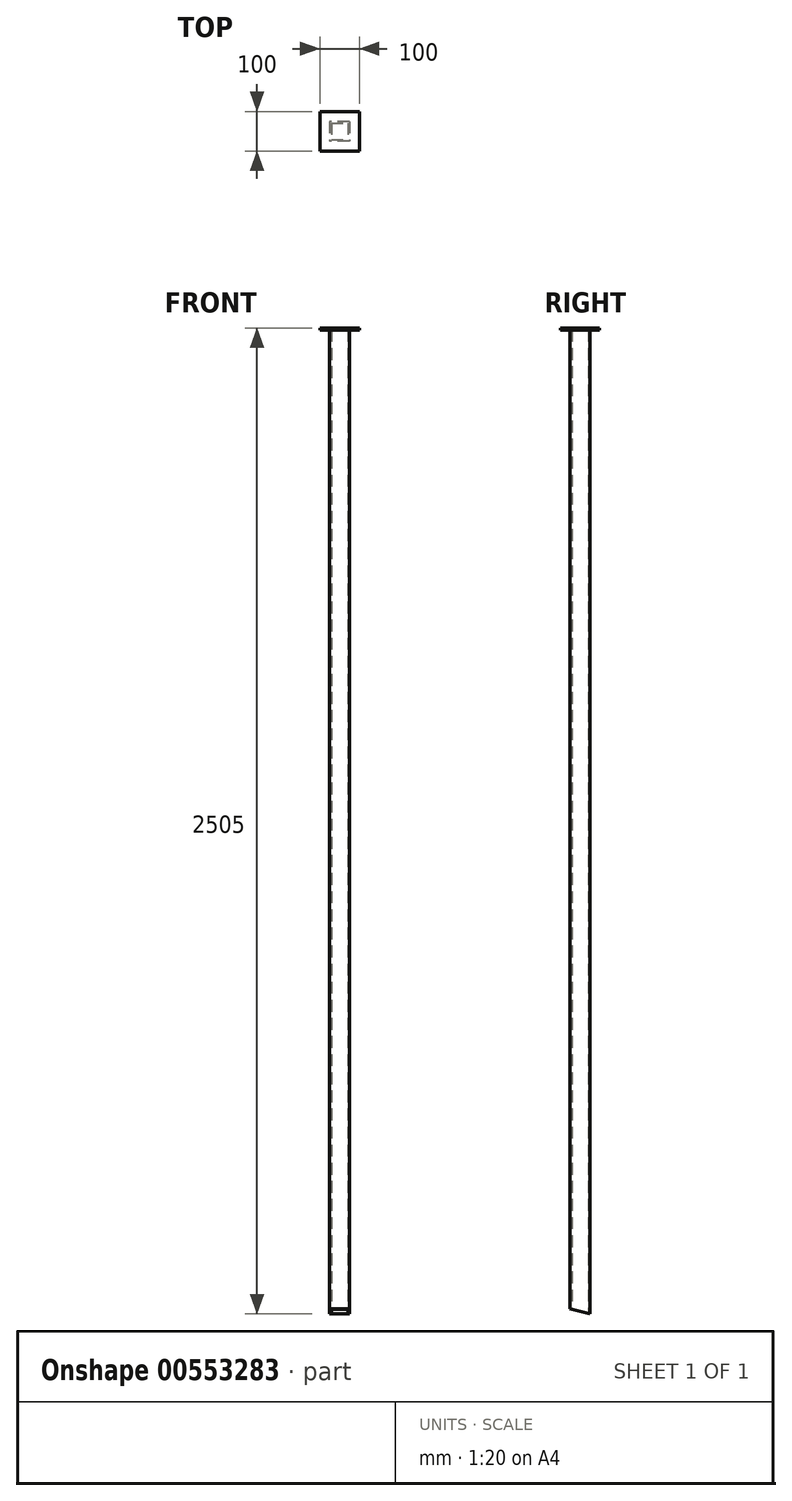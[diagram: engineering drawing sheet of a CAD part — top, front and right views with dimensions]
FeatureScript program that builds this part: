
annotation { "Feature Type Name" : "Feature", "Feature Type Description" : "" }
export const myFeature = defineFeature(function(context is Context, id is Id, definition is map)
    precondition{}
    {
        {
            var Q0;
            Q0=qCreatedBy(makeId("Top.planeOp"),FACE);
            var sketch = newSketch(context, id + "F0", { "sketchPlane" : qUnion([Q0])});
            skLineSegment(sketch, "E0.bottom", {"start": v(25, -25) * mm, "end": v(-25, -25) * mm});
            skLineSegment(sketch, "E0.top", {"start": v(25, 25) * mm, "end": v(-25, 25) * mm});
            skLineSegment(sketch, "E0.left", {"start": v(25, -25) * mm, "end": v(25, 25) * mm});
            skLineSegment(sketch, "E0.right", {"start": v(-25, -25) * mm, "end": v(-25, 25) * mm});
            skPoint(sketch, "E0.middle", {"position": v(0, 0) * mm});
            skLineSegment(sketch, "E1.bottom", {"start": v(21, -21) * mm, "end": v(-21, -21) * mm});
            skLineSegment(sketch, "E1.top", {"start": v(21, 21) * mm, "end": v(-21, 21) * mm});
            skLineSegment(sketch, "E1.left", {"start": v(21, -21) * mm, "end": v(21, 21) * mm});
            skLineSegment(sketch, "E1.right", {"start": v(-21, -21) * mm, "end": v(-21, 21) * mm});
            skSolve(sketch);
        }
        {
            var Q0;
            Q0=makeQuery(id+"F0.imprint","IMPRINT",FACE,{"disambiguationData":[TD([[makeQuery(id+"F0.imprint","IMPRINT",EDGE,{"derivedFrom":sQuery(id+"F0.wireOp",EDGE,"E0.bottom")}),-1.0]])]});
            extrude(context, id + "F1", {"entities" : qUnion([Q0]), "depth" : 2500 * mm, "offsetDistance" : 25 * mm});
        }
        {
            var Q0;
            Q0=makeQuery(id+"F1.opExtrude","CAP_FACE",FACE,{"disambiguationData":[OSD([sQuery(id+"F0.wireOp",EDGE,"E0.bottom"),sQuery(id+"F0.wireOp",EDGE,"E0.top"),sQuery(id+"F0.wireOp",EDGE,"E0.left"),sQuery(id+"F0.wireOp",EDGE,"E0.right"),sQuery(id+"F0.wireOp",EDGE,"E1.bottom"),sQuery(id+"F0.wireOp",EDGE,"E1.top"),sQuery(id+"F0.wireOp",EDGE,"E1.left"),sQuery(id+"F0.wireOp",EDGE,"E1.right")])],"isStart":false});
            var sketch = newSketch(context, id + "F2", { "sketchPlane" : qUnion([Q0])});
            skLineSegment(sketch, "E2.bottom", {"start": v(50, 50) * mm, "end": v(-50, 50) * mm});
            skLineSegment(sketch, "E2.top", {"start": v(50, -50) * mm, "end": v(-50, -50) * mm});
            skLineSegment(sketch, "E2.left", {"start": v(50, 50) * mm, "end": v(50, -50) * mm});
            skLineSegment(sketch, "E2.right", {"start": v(-50, 50) * mm, "end": v(-50, -50) * mm});
            skPoint(sketch, "E2.middle", {"position": v(0, 0) * mm});
            skSolve(sketch);
        }
        {
            var Q0;
            Q0=makeQuery(id+"F2.imprint","IMPRINT",FACE,{"disambiguationData":[TD([[makeQuery(id+"F2.imprint","IMPRINT",EDGE,{"derivedFrom":sQuery(id+"F2.wireOp",EDGE,"E2.bottom")}),1.0]])]});
            var Q1;
            Q1=makeQuery(id+"F2.imprint","IMPRINT",FACE,{"disambiguationData":[TD([[makeQuery(id+"F2.imprint","IMPRINT",EDGE,{"derivedFrom":makeQuery(id+"F1.opExtrude","CAP_EDGE",EDGE,{"disambiguationData":[OSD([sQuery(id+"F0.wireOp",EDGE,"E0.bottom")])],"isStart":false})}),-1.0]])]});
            var Q2;
            Q2=makeQuery(id+"F2.imprint","IMPRINT",FACE,{"disambiguationData":[TD([[makeQuery(id+"F2.imprint","IMPRINT",EDGE,{"derivedFrom":makeQuery(id+"F1.opExtrude","CAP_EDGE",EDGE,{"disambiguationData":[OSD([sQuery(id+"F0.wireOp",EDGE,"E1.bottom")])],"isStart":false})}),-1.0]])]});
            extrude(context, id + "F3", {"entities" : qUnion([Q0, Q1, Q2]), "operationType" : NewBodyOperationType.ADD, "depth" : 5 * mm, "offsetDistance" : 25 * mm});
        }
        {
            var Q0;
            Q0=makeQuery(id+"F1.opExtrude","SWEPT_FACE",FACE,{"disambiguationData":[OSD([sQuery(id+"F0.wireOp",EDGE,"E0.right")])]});
            var sketch = newSketch(context, id + "F4", { "sketchPlane" : qUnion([Q0])});
            skLineSegment(sketch, "E3", {"start": v(-25, 0) * mm, "end": v(25, 13.09) * mm});
            skLineSegment(sketch, "E4", {"start": v(25, 13.09) * mm, "end": v(25, 0) * mm});
            skLineSegment(sketch, "E5", {"start": v(25, 0) * mm, "end": v(-25, 0) * mm});
            skSolve(sketch);
        }
        {
            var Q0;
            Q0=makeQuery(id+"F4.imprint","IMPRINT",FACE,{"disambiguationData":[TD([[makeQuery(id+"F4.imprint","IMPRINT",EDGE,{"derivedFrom":sQuery(id+"F4.wireOp",EDGE,"E3")}),-1.0]])]});
            extrude(context, id + "F5", {"entities" : qUnion([Q0]), "operationType" : NewBodyOperationType.REMOVE, "oppositeDirection" : true, "depth" : 50 * mm, "offsetDistance" : 25 * mm});
        }
    });
